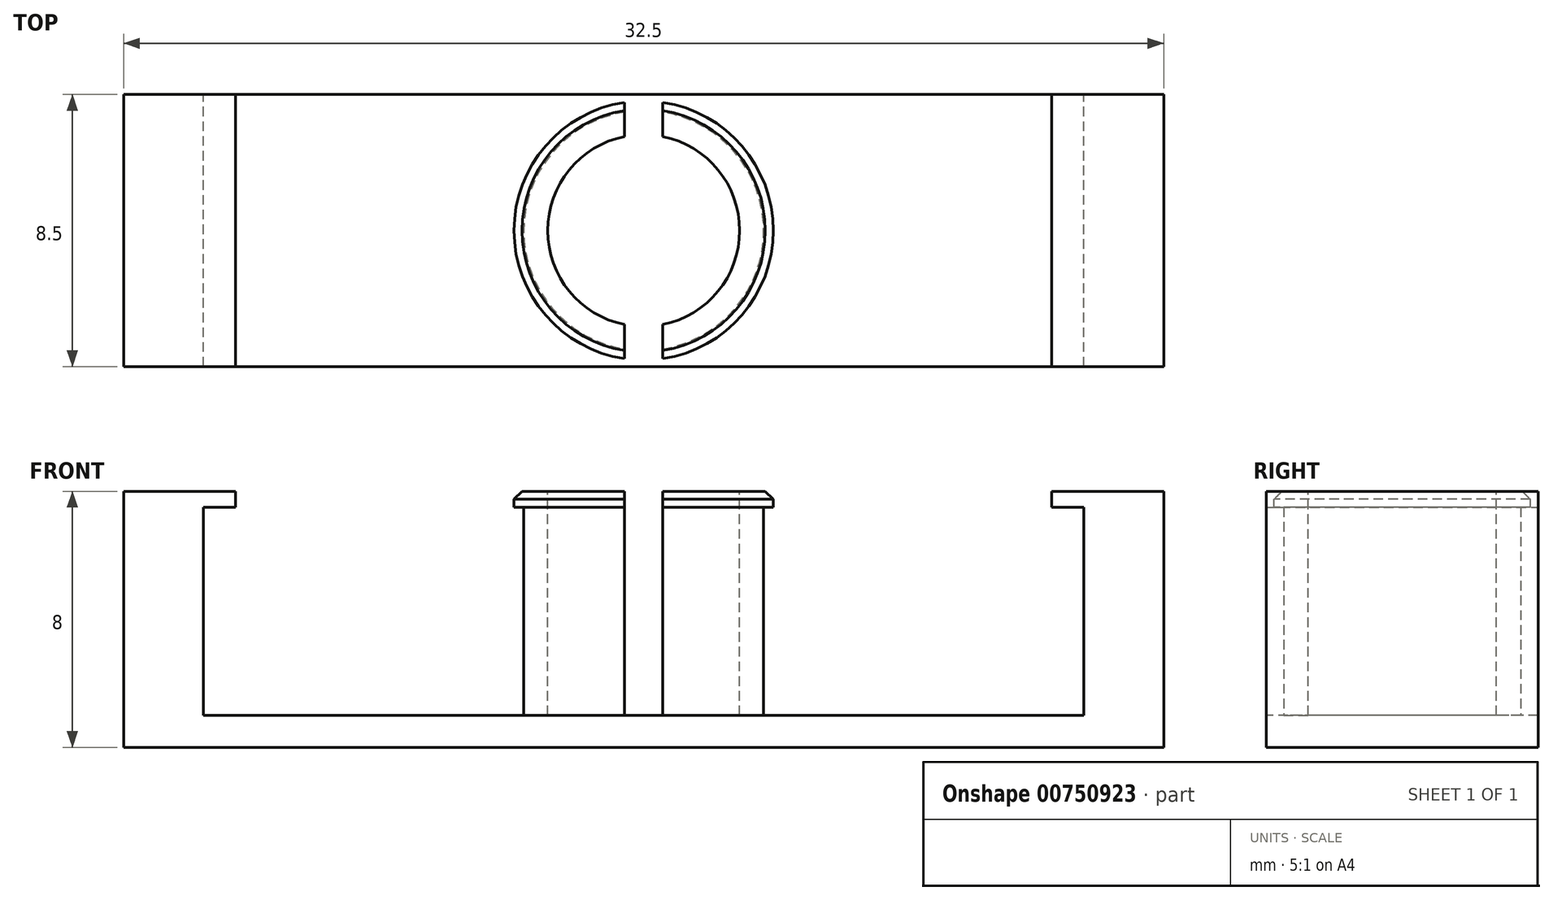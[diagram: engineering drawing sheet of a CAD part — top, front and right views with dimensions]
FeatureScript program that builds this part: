
annotation { "Feature Type Name" : "Feature", "Feature Type Description" : "" }
export const myFeature = defineFeature(function(context is Context, id is Id, definition is map)
    precondition{}
    {
        {
            var Q0;
            Q0=qCreatedBy(makeId("Top.planeOp"),FACE);
            var sketch = newSketch(context, id + "F0", { "sketchPlane" : qUnion([Q0])});
            skLineSegment(sketch, "E0", {"start": v(0, 0) * mm, "end": v(27.5, 0) * mm});
            skLineSegment(sketch, "E1", {"start": v(0, 0) * mm, "end": v(0, 8.5) * mm});
            skLineSegment(sketch, "E2.bottom", {"start": v(0, 8.5) * mm, "end": v(27.5, 8.5) * mm});
            skLineSegment(sketch, "E2.left", {"start": v(0, 8.5) * mm, "end": v(0, 0) * mm});
            skLineSegment(sketch, "E2.right", {"start": v(27.5, 8.5) * mm, "end": v(27.5, 0) * mm});
            skLineSegment(sketch, "E3", {"start": v(13.75, 0) * mm, "end": v(13.75, 8.5) * mm});
            skCircle(sketch, "E4", {"center": v(13.75, 4.25) * mm, "radius": 3.75 * mm});
            skSolve(sketch);
        }
        {
            var Q0;
            Q0 = qSketchRegion(id + "F0", true);
            var Q1;
            {var subQ0=sQuery(id+"F0.wireOp",EDGE,"E4");var subQ1=sQuery(id+"F0.wireOp",EDGE,"E3");var subQ2=makeQuery(id+"F0.imprint","INTERSECT",VERTEX,{"disambiguationData":[OD(0.0)],"derivedFrom":[subQ1,subQ0]});Q1=makeQuery(id+"F0.imprint","IMPRINT",FACE,{"disambiguationData":[TD([[makeQuery(id+"F0.imprint","IMPRINT",EDGE,{"disambiguationData":[TD([[subQ2,-1.0]])],"derivedFrom":subQ1}),1.0]])]});}
            var Q2;
            {var subQ0=sQuery(id+"F0.wireOp",EDGE,"E4");var subQ1=sQuery(id+"F0.wireOp",EDGE,"E3");var subQ2=makeQuery(id+"F0.imprint","INTERSECT",VERTEX,{"disambiguationData":[OD(0.0)],"derivedFrom":[subQ1,subQ0]});Q2=makeQuery(id+"F0.imprint","IMPRINT",FACE,{"disambiguationData":[TD([[makeQuery(id+"F0.imprint","IMPRINT",EDGE,{"disambiguationData":[TD([[subQ2,-1.0]])],"derivedFrom":subQ1}),-1.0]])]});}
            extrude(context, id + "F1", {"entities" : qUnion([Q0, Q1, Q2]), "depth" : 1 * mm, "offsetDistance" : 25 * mm});
        }
        {
            var Q0;
            Q0=qCreatedBy(makeId("Top.planeOp"),FACE);
            var sketch = newSketch(context, id + "F2", { "sketchPlane" : qUnion([Q0])});
            skLineSegment(sketch, "E5", {"start": v(0, 0) * mm, "end": v(-2.5, 0) * mm});
            skLineSegment(sketch, "E6.bottom", {"start": v(-2.5, 0) * mm, "end": v(0, 0) * mm});
            skLineSegment(sketch, "E6.top", {"start": v(-2.5, 8.5) * mm, "end": v(0, 8.5) * mm});
            skLineSegment(sketch, "E6.left", {"start": v(-2.5, 0) * mm, "end": v(-2.5, 8.5) * mm});
            skLineSegment(sketch, "E6.right", {"start": v(0, 0) * mm, "end": v(0, 8.5) * mm});
            skLineSegment(sketch, "E7", {"start": v(0, 0) * mm, "end": v(13.75, 0) * mm});
            skLineSegment(sketch, "E8", {"start": v(13.75, 0) * mm, "end": v(13.75, 8.5) * mm});
            skLineSegment(sketch, "E9.MirrorCS", {"start": v(30, 8.5) * mm, "end": v(27.5, 8.5) * mm});
            skLineSegment(sketch, "E10.MirrorCS", {"start": v(30, 0) * mm, "end": v(30, 8.5) * mm});
            skLineSegment(sketch, "E11.MirrorCS", {"start": v(30, 0) * mm, "end": v(27.5, 0) * mm});
            skLineSegment(sketch, "E12.MirrorCS", {"start": v(27.5, 0) * mm, "end": v(27.5, 8.5) * mm});
            skCircle(sketch, "E13", {"center": v(13.75, 4.25) * mm, "radius": 3.75 * mm});
            skSolve(sketch);
        }
        {
            var Q0;
            Q0 = qSketchRegion(id + "F2", true);
            extrude(context, id + "F3", {"entities" : qUnion([Q0]), "operationType" : NewBodyOperationType.ADD, "depth" : 8 * mm, "offsetDistance" : 25 * mm});
        }
        {
            var Q0;
            Q0=qCreatedBy(makeId("Top.planeOp"),FACE);
            cPlane(context, id + "F4", {"entities" : qUnion([Q0]), "cplaneType" : CPlaneType.OFFSET, "offset" : 8 * mm, "width" : 150 * mm, "height" : 150 * mm});
        }
        {
            var Q0;
            Q0=qCreatedBy(id+"F4.planeOp",FACE);
            var sketch = newSketch(context, id + "F5", { "sketchPlane" : qUnion([Q0])});
            skLineSegment(sketch, "E14", {"start": v(0, 0) * mm, "end": v(0, 8.5) * mm});
            skLineSegment(sketch, "E15", {"start": v(0, 0) * mm, "end": v(13.75, 0) * mm});
            skLineSegment(sketch, "E16", {"start": v(13.75, 0) * mm, "end": v(13.75, 8.5) * mm});
            skLineSegment(sketch, "E17.MirrorCS", {"start": v(27.5, 0) * mm, "end": v(27.5, 8.5) * mm});
            skLineSegment(sketch, "E18", {"start": v(0, 8.5) * mm, "end": v(1, 8.5) * mm});
            skLineSegment(sketch, "E19.bottom", {"start": v(0, 0) * mm, "end": v(1, 0) * mm});
            skLineSegment(sketch, "E19.right", {"start": v(1, 0) * mm, "end": v(1, 8.5) * mm});
            skLineSegment(sketch, "E20.MirrorCS", {"start": v(27.5, 8.5) * mm, "end": v(26.5, 8.5) * mm});
            skLineSegment(sketch, "E21.MirrorCS", {"start": v(26.5, 0) * mm, "end": v(26.5, 8.5) * mm});
            skLineSegment(sketch, "E22.MirrorCS", {"start": v(27.5, 0) * mm, "end": v(26.5, 0) * mm});
            skCircle(sketch, "E23", {"center": v(13.75, 4.25) * mm, "radius": 4.05 * mm});
            skSolve(sketch);
        }
        {
            var Q0;
            {var subQ0=sQuery(id+"F5.wireOp",EDGE,"E23");var subQ1=sQuery(id+"F5.wireOp",EDGE,"E16");var subQ2=makeQuery(id+"F5.imprint","INTERSECT",VERTEX,{"disambiguationData":[OD(0.0)],"derivedFrom":[subQ1,subQ0]});var subQ4=makeQuery(id+"F5.imprint","IMPRINT",EDGE,{"disambiguationData":[TD([[subQ2,-1.0]])],"derivedFrom":subQ1});var subQ5=sQuery(id+"F5.wireOp",EDGE,"E14");Q0=qUnion([makeQuery(id+"F5.imprint","IMPRINT",FACE,{"disambiguationData":[TD([[makeQuery(id+"F5.imprint","IMPRINT",EDGE,{"derivedFrom":sQuery(id+"F5.wireOp",EDGE,"E17.MirrorCS")}),1.0]])]}),makeQuery(id+"F5.imprint","IMPRINT",FACE,{"disambiguationData":[TD([[makeQuery(id+"F5.imprint","IMPRINT",EDGE,{"derivedFrom":subQ5}),-1.0]])]}),makeQuery(id+"F5.imprint","IMPRINT",FACE,{"disambiguationData":[TD([[subQ4,1.0]])]}),makeQuery(id+"F5.imprint","IMPRINT",FACE,{"disambiguationData":[TD([[subQ4,-1.0]])]})]);}
            extrude(context, id + "F6", {"entities" : qUnion([Q0]), "operationType" : NewBodyOperationType.ADD, "oppositeDirection" : true, "depth" : .5 * mm, "offsetDistance" : 25 * mm});
        }
        {
            var Q0;
            Q0=qCreatedBy(id+"F4.planeOp",FACE);
            cPlane(context, id + "F7", {"entities" : qUnion([Q0]), "cplaneType" : CPlaneType.OFFSET, "offset" : 2 * mm, "width" : 150 * mm, "height" : 150 * mm});
        }
        {
            var Q0;
            Q0=qCreatedBy(id+"F7.planeOp",FACE);
            var sketch = newSketch(context, id + "F8", { "sketchPlane" : qUnion([Q0])});
            skLineSegment(sketch, "E24", {"start": v(0, 0) * mm, "end": v(13.75, 0) * mm});
            skLineSegment(sketch, "E25", {"start": v(13.75, 0) * mm, "end": v(13.75, 8.5) * mm});
            skCircle(sketch, "E26", {"center": v(13.75, 4.25) * mm, "radius": 3 * mm});
            skLineSegment(sketch, "E27", {"start": v(13.75, 0) * mm, "end": v(14.35, 0) * mm});
            skLineSegment(sketch, "E28.bottom", {"start": v(14.35, 0) * mm, "end": v(13.75, 0) * mm});
            skLineSegment(sketch, "E28.top", {"start": v(14.35, 4.25) * mm, "end": v(13.75, 4.25) * mm});
            skLineSegment(sketch, "E28.left", {"start": v(14.35, 0) * mm, "end": v(14.35, 4.25) * mm});
            skLineSegment(sketch, "E28.right", {"start": v(13.75, 0) * mm, "end": v(13.75, 4.25) * mm});
            skLineSegment(sketch, "E29.bottom", {"start": v(13.75, 8.5) * mm, "end": v(14.35, 8.5) * mm});
            skLineSegment(sketch, "E29.top", {"start": v(13.75, 4.25) * mm, "end": v(14.35, 4.25) * mm});
            skLineSegment(sketch, "E29.left", {"start": v(13.75, 8.5) * mm, "end": v(13.75, 4.25) * mm});
            skLineSegment(sketch, "E29.right", {"start": v(14.35, 8.5) * mm, "end": v(14.35, 4.25) * mm});
            skLineSegment(sketch, "E30.MirrorCS", {"start": v(13.15, 0) * mm, "end": v(13.75, 0) * mm});
            skLineSegment(sketch, "E31.MirrorCS", {"start": v(13.15, 0) * mm, "end": v(13.15, 4.25) * mm});
            skLineSegment(sketch, "E32.MirrorCS", {"start": v(13.75, 8.5) * mm, "end": v(13.15, 8.5) * mm});
            skLineSegment(sketch, "E33.MirrorCS", {"start": v(13.15, 8.5) * mm, "end": v(13.15, 4.25) * mm});
            skSolve(sketch);
        }
        {
            var Q0;
            {var subQ0=sQuery(id+"F8.wireOp",EDGE,"E26");var subQ1=sQuery(id+"F8.wireOp",EDGE,"E25");var subQ2=makeQuery(id+"F8.imprint","INTERSECT",VERTEX,{"disambiguationData":[OD(0.0)],"derivedFrom":[subQ1,subQ0]});var subQ3=sQuery(id+"F8.wireOp",EDGE,"E31.MirrorCS");var subQ4=makeQuery(id+"F8.imprint","INTERSECT",VERTEX,{"derivedFrom":[subQ0,subQ3]});var subQ5=makeQuery(id+"F8.imprint","IMPRINT",EDGE,{"disambiguationData":[TD([[subQ2,1.0]])],"derivedFrom":subQ0});var subQ6=sQuery(id+"F8.wireOp",EDGE,"E28.top");var subQ13=makeQuery(id+"F8.imprint","IMPRINT",EDGE,{"disambiguationData":[TD([[subQ2,-1.0]])],"derivedFrom":subQ1});var subQ17=sQuery(id+"F8.wireOp",EDGE,"E28.left");var subQ18=makeQuery(id+"F8.imprint","INTERSECT",VERTEX,{"derivedFrom":[subQ0,subQ17]});var subQ24=sQuery(id+"F8.wireOp",EDGE,"E27");var subQ29=makeQuery(id+"F8.imprint","IMPRINT",EDGE,{"derivedFrom":subQ6});var subQ31=sQuery(id+"F8.wireOp",EDGE,"E32.MirrorCS");var subQ32=sQuery(id+"F8.wireOp",EDGE,"E29.bottom");Q0=qUnion([makeQuery(id+"F8.imprint","IMPRINT",FACE,{"disambiguationData":[TD([[makeQuery(id+"F8.imprint","IMPRINT",EDGE,{"derivedFrom":subQ24}),1.0]])]}),makeQuery(id+"F8.imprint","IMPRINT",FACE,{"disambiguationData":[TD([[makeQuery(id+"F8.imprint","IMPRINT",EDGE,{"derivedFrom":subQ32}),-1.0]])]}),makeQuery(id+"F8.imprint","IMPRINT",FACE,{"disambiguationData":[TD([[subQ29,1.0]])]}),makeQuery(id+"F8.imprint","IMPRINT",FACE,{"disambiguationData":[TD([[makeQuery(id+"F8.imprint","IMPRINT",EDGE,{"disambiguationData":[TD([[subQ4,1.0]])],"derivedFrom":subQ0}),1.0]])]}),makeQuery(id+"F8.imprint","IMPRINT",FACE,{"disambiguationData":[TD([[makeQuery(id+"F8.imprint","IMPRINT",EDGE,{"derivedFrom":subQ31}),1.0]])]}),makeQuery(id+"F8.imprint","IMPRINT",FACE,{"disambiguationData":[TD([[subQ29,-1.0]])]}),makeQuery(id+"F8.imprint","IMPRINT",FACE,{"disambiguationData":[TD([[subQ5,-1.0]])]}),makeQuery(id+"F8.imprint","IMPRINT",FACE,{"disambiguationData":[TD([[makeQuery(id+"F8.imprint","IMPRINT",EDGE,{"disambiguationData":[TD([[subQ18,-1.0]])],"derivedFrom":subQ0}),1.0]])]}),makeQuery(id+"F8.imprint","IMPRINT",FACE,{"disambiguationData":[TD([[subQ13,1.0]])]})]);}
            extrude(context, id + "F9", {"entities" : qUnion([Q0]), "operationType" : NewBodyOperationType.REMOVE, "oppositeDirection" : true, "depth" : 9 * mm, "offsetDistance" : 25 * mm});
        }
        {
            var Q0;
            {var subQ0=sQuery(id+"F5.wireOp",EDGE,"E23");Q0=makeQuery(id+"F9.boolean.opBoolean","SPLIT",EDGE,{"disambiguationData":[TD([makeQuery(id+"F9.opExtrude","SWEPT_FACE",FACE,{"disambiguationData":[OSD([sQuery(id+"F8.wireOp",EDGE,"E31.MirrorCS")])]})])],"derivedFrom":makeQuery(id+"F6.opExtrude","CAP_EDGE",EDGE,{"disambiguationData":[OSD([subQ0])],"isStart":true})});}
            var Q1;
            {var subQ0=sQuery(id+"F5.wireOp",EDGE,"E23");Q1=makeQuery(id+"F9.boolean.opBoolean","SPLIT",EDGE,{"disambiguationData":[TD([makeQuery(id+"F9.opExtrude","SWEPT_FACE",FACE,{"disambiguationData":[OSD([sQuery(id+"F8.wireOp",EDGE,"E28.left")])]})])],"derivedFrom":makeQuery(id+"F6.opExtrude","CAP_EDGE",EDGE,{"disambiguationData":[OSD([subQ0])],"isStart":true})});}
            chamfer(context, id + "F10", {"entities" : qUnion([Q0, Q1]), "width" : .25 * mm, "tangentPropagation" : true});
        }
    });
